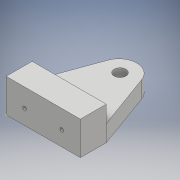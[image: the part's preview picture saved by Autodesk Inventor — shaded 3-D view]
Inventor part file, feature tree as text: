
AUTODESK INVENTOR PART (.ipt)
format: ipt  version: 2017 (Build 210142000, 142)  size: 128,000 bytes
history: native  units: mm
features: sketch x5, extrude x3
ambient origin geometry x8: Origin, YZ Plane, XZ Plane, XY Plane, X Axis, Y Axis, Z Axis, Center Point
bodies: Solid1 (feature_tree)
feature tree (8):
  sketch  "Sketch1"  dims[d9=4.5mm d10=0.0mm d11=4.5mm d12=0.0mm]
  sketch  "Sketch2"  dims[d13=1.0mm d14=1.0mm]
  sketch  "Sketch3"  dims[d15=5.5mm d16=0.0mm d17=7.0mm]
  extrude  "Extrusion1"  Depth=4.5mm TaperAngle=0.0deg
  extrude  "Extrusion2"  Depth=1.0mm
  extrude  "Extrusion3"  Depth=7.0mm
  sketch  "Sketch4"  dims[d18=6.999813mm]
  sketch  "Sketch5"  dims[d19=20.7mm d23=90.0deg d24=90.0deg d25=10.0mm d26=16.0mm d27=12.217305mm d28=16.0mm d29=19.198622mm d30=10.0mm d33=5.0mm d34=5.0mm]
